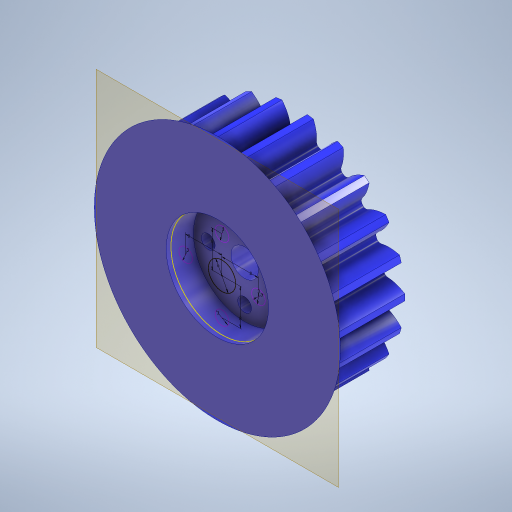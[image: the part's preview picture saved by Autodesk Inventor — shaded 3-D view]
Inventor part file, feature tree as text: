
AUTODESK INVENTOR PART (.ipt)
format: ipt  version: 2024.2 (Build 282272000, 272)  size: 1,037,824 bytes
history: native  units: mm
features: sketch x8, extrude x7, other x5, loft x2, pattern_circular x1
ambient origin geometry x8: Origin, YZ Plane, XZ Plane, XY Plane, X Axis, Y Axis, Z Axis, Center Point
bodies: Body1 (feature_tree)
feature tree (23):
  other  "Твердое тело1"
  sketch  "Sketch1"  dims[d0=16.0mm d1=0.0mm d4=0.0mm d5=0.0mm d6=220.0mm d7=360.0deg d9=6.0mm d10=3.0mm d11=3.0mm d12=3.0mm d13=3.0mm d14=8.0mm d15=8.0mm d16=8.0mm d17=8.0mm d18=3.0mm d19=10.0mm d20=0.0mm d21=0.0mm d22=3.0mm d23=52.0mm d24=0.0mm d25=90.0deg d26=0.0mm d27=90.0deg d28=22.8mm d29=7.5mm d30=0.0mm d31=3.0mm d32=0.0mm d33=3.0mm d39=22.5mm d40=5.0mm d41=0.0mm d42=1.0mm d47=0.0mm d48=90.0deg d49=0.0mm d50=90.0deg d51=1.0mm d52=0.0mm]
  extrude  "Выдавливание1"  TaperAngle=0.0deg  [1 undecoded]
  extrude  "Выдавливание2"  TaperAngle=0.0deg  [1 undecoded]
  pattern_circular  "Круговой массив1"  Count=22 Angle=360.0deg
  extrude  "Выдавливание3"  Depth=1.0mm
  other  "РабПлоскость1"
  extrude  "Выдавливание6"  Depth=1.0mm
  sketch  "Эскиз8"
  other  "РабПлоскость3"
  loft  "Лофт4"
  extrude  "Выдавливание7"  Depth=1.0mm
  loft  "Лофт1"
  extrude  "Выдавливание4"  Depth=1.0mm
  extrude  "Выдавливание5"  Depth=1.0mm
  other  "РабПлоскость2"
  sketch  "Эскиз2"
  sketch  "Эскиз3"
  sketch  "Эскиз4"
  sketch  "Эскиз7"
  sketch  "Эскиз9"
  other  "Ребра2"
  sketch  "Эскиз10"
note: 2 required parameter values undecoded (feature->parameter linkage not recoverable at this tier; creation-order binding heuristic only, values carry confidence <= 0.55)
